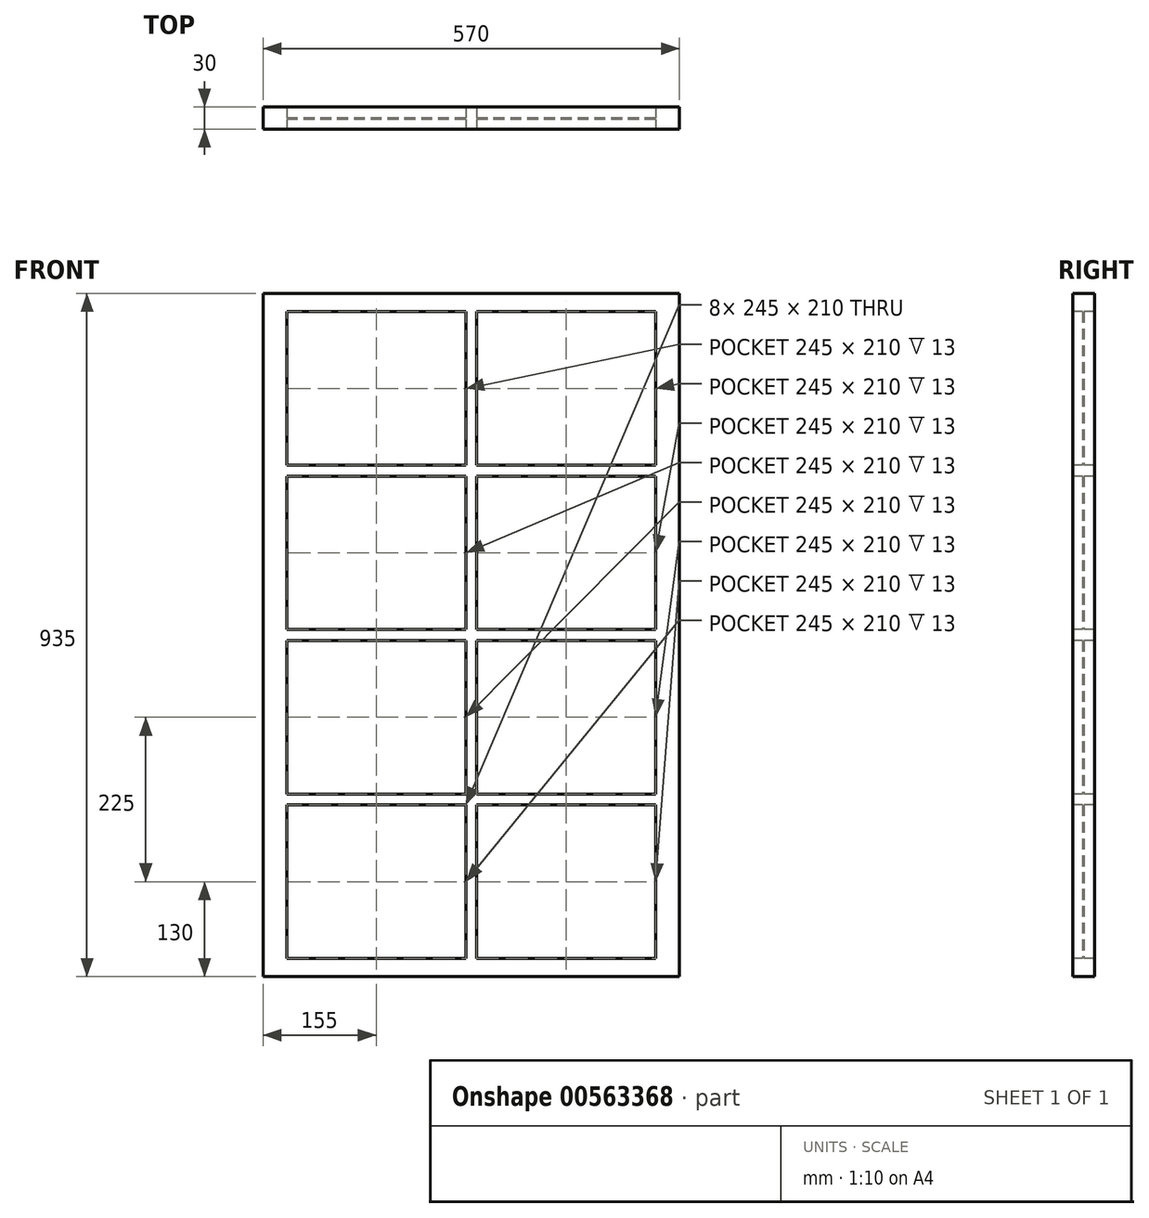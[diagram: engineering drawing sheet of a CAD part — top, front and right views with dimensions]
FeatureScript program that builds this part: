
annotation { "Feature Type Name" : "Feature", "Feature Type Description" : "" }
export const myFeature = defineFeature(function(context is Context, id is Id, definition is map)
    precondition{}
    {
        {
            var Q0;
            Q0=qCreatedBy(makeId("Front.planeOp"),FACE);
            var sketch = newSketch(context, id + "F0", { "sketchPlane" : qUnion([Q0])});
            skLineSegment(sketch, "E0.bottom", {"start": v(-285, 467.5) * mm, "end": v(285, 467.5) * mm});
            skLineSegment(sketch, "E0.top", {"start": v(-285, -467.5) * mm, "end": v(285, -467.5) * mm});
            skLineSegment(sketch, "E0.left", {"start": v(-285, 467.5) * mm, "end": v(-285, -467.5) * mm});
            skLineSegment(sketch, "E0.right", {"start": v(285, 467.5) * mm, "end": v(285, -467.5) * mm});
            skPoint(sketch, "E0.middle", {"position": v(0, 0) * mm});
            skLineSegment(sketch, "E1.bottom", {"start": v(-7.5, 442.5) * mm, "end": v(-252.5, 442.5) * mm});
            skLineSegment(sketch, "E1.top", {"start": v(-7.5, 232.5) * mm, "end": v(-252.5, 232.5) * mm});
            skLineSegment(sketch, "E1.left", {"start": v(-7.5, 442.5) * mm, "end": v(-7.5, 232.5) * mm});
            skLineSegment(sketch, "E1.right", {"start": v(-252.5, 442.5) * mm, "end": v(-252.5, 232.5) * mm});
            skPoint(sketch, "E1.middle", {"position": v(-130, 337.5) * mm});
            skLineSegment(sketch, "E2.0.1.0", {"start": v(-7.5, 217.5) * mm, "end": v(-252.5, 217.5) * mm});
            skLineSegment(sketch, "E2.0.1.1", {"start": v(-252.5, 217.5) * mm, "end": v(-252.5, 7.5) * mm});
            skLineSegment(sketch, "E2.0.1.2", {"start": v(-7.5, 217.5) * mm, "end": v(-7.5, 7.5) * mm});
            skLineSegment(sketch, "E2.0.1.3", {"start": v(-7.5, 7.5) * mm, "end": v(-252.5, 7.5) * mm});
            skLineSegment(sketch, "E2.0.2.0", {"start": v(-7.5, -7.5) * mm, "end": v(-252.5, -7.5) * mm});
            skLineSegment(sketch, "E2.0.2.1", {"start": v(-252.5, -7.5) * mm, "end": v(-252.5, -217.5) * mm});
            skLineSegment(sketch, "E2.0.2.2", {"start": v(-7.5, -7.5) * mm, "end": v(-7.5, -217.5) * mm});
            skLineSegment(sketch, "E2.0.2.3", {"start": v(-7.5, -217.5) * mm, "end": v(-252.5, -217.5) * mm});
            skLineSegment(sketch, "E2.0.3.0", {"start": v(-7.5, -232.5) * mm, "end": v(-252.5, -232.5) * mm});
            skLineSegment(sketch, "E2.0.3.1", {"start": v(-252.5, -232.5) * mm, "end": v(-252.5, -442.5) * mm});
            skLineSegment(sketch, "E2.0.3.2", {"start": v(-7.5, -232.5) * mm, "end": v(-7.5, -442.5) * mm});
            skLineSegment(sketch, "E2.0.3.3", {"start": v(-7.5, -442.5) * mm, "end": v(-252.5, -442.5) * mm});
            skLineSegment(sketch, "E2.1.0.0", {"start": v(252.5, 442.5) * mm, "end": v(7.5, 442.5) * mm});
            skLineSegment(sketch, "E2.1.0.1", {"start": v(7.5, 442.5) * mm, "end": v(7.5, 232.5) * mm});
            skLineSegment(sketch, "E2.1.0.2", {"start": v(252.5, 442.5) * mm, "end": v(252.5, 232.5) * mm});
            skLineSegment(sketch, "E2.1.0.3", {"start": v(252.5, 232.5) * mm, "end": v(7.5, 232.5) * mm});
            skLineSegment(sketch, "E2.1.1.0", {"start": v(252.5, 217.5) * mm, "end": v(7.5, 217.5) * mm});
            skLineSegment(sketch, "E2.1.1.1", {"start": v(7.5, 217.5) * mm, "end": v(7.5, 7.5) * mm});
            skLineSegment(sketch, "E2.1.1.2", {"start": v(252.5, 217.5) * mm, "end": v(252.5, 7.5) * mm});
            skLineSegment(sketch, "E2.1.1.3", {"start": v(252.5, 7.5) * mm, "end": v(7.5, 7.5) * mm});
            skLineSegment(sketch, "E2.1.2.0", {"start": v(252.5, -7.5) * mm, "end": v(7.5, -7.5) * mm});
            skLineSegment(sketch, "E2.1.2.1", {"start": v(7.5, -7.5) * mm, "end": v(7.5, -217.5) * mm});
            skLineSegment(sketch, "E2.1.2.2", {"start": v(252.5, -7.5) * mm, "end": v(252.5, -217.5) * mm});
            skLineSegment(sketch, "E2.1.2.3", {"start": v(252.5, -217.5) * mm, "end": v(7.5, -217.5) * mm});
            skLineSegment(sketch, "E2.1.3.0", {"start": v(252.5, -232.5) * mm, "end": v(7.5, -232.5) * mm});
            skLineSegment(sketch, "E2.1.3.1", {"start": v(7.5, -232.5) * mm, "end": v(7.5, -442.5) * mm});
            skLineSegment(sketch, "E2.1.3.2", {"start": v(252.5, -232.5) * mm, "end": v(252.5, -442.5) * mm});
            skLineSegment(sketch, "E2.1.3.3", {"start": v(252.5, -442.5) * mm, "end": v(7.5, -442.5) * mm});
            skLineSegment(sketch, "E2.direction1", {"start": v(-252.5, 232.5) * mm, "end": v(7.5, 232.5) * mm, "construction": true});
            skLineSegment(sketch, "E2.direction2", {"start": v(-252.5, 232.5) * mm, "end": v(-252.5, 7.5) * mm, "construction": true});
            skSolve(sketch);
        }
        {
            var Q0;
            Q0=makeQuery(id+"F0.imprint","IMPRINT",FACE,{"disambiguationData":[TD([[makeQuery(id+"F0.imprint","IMPRINT",EDGE,{"derivedFrom":sQuery(id+"F0.wireOp",EDGE,"E0.bottom")}),-1.0]])]});
            extrude(context, id + "F1", {"entities" : qUnion([Q0]), "oppositeDirection" : true, "depth" : 30 * mm, "offsetDistance" : 25 * mm});
        }
        {
            var Q0;
            Q0=makeQuery(id+"F1.opExtrude","CAP_FACE",FACE,{"disambiguationData":[OSD([sQuery(id+"F0.wireOp",EDGE,"E0.bottom"),sQuery(id+"F0.wireOp",EDGE,"E0.top"),sQuery(id+"F0.wireOp",EDGE,"E0.left"),sQuery(id+"F0.wireOp",EDGE,"E0.right"),sQuery(id+"F0.wireOp",EDGE,"E1.bottom"),sQuery(id+"F0.wireOp",EDGE,"E1.top"),sQuery(id+"F0.wireOp",EDGE,"E1.left"),sQuery(id+"F0.wireOp",EDGE,"E1.right"),sQuery(id+"F0.wireOp",EDGE,"E2.0.1.0"),sQuery(id+"F0.wireOp",EDGE,"E2.0.1.1"),sQuery(id+"F0.wireOp",EDGE,"E2.0.1.2"),sQuery(id+"F0.wireOp",EDGE,"E2.0.1.3"),sQuery(id+"F0.wireOp",EDGE,"E2.0.2.0"),sQuery(id+"F0.wireOp",EDGE,"E2.0.2.1"),sQuery(id+"F0.wireOp",EDGE,"E2.0.2.2"),sQuery(id+"F0.wireOp",EDGE,"E2.0.2.3"),sQuery(id+"F0.wireOp",EDGE,"E2.0.3.0"),sQuery(id+"F0.wireOp",EDGE,"E2.0.3.1"),sQuery(id+"F0.wireOp",EDGE,"E2.0.3.2"),sQuery(id+"F0.wireOp",EDGE,"E2.0.3.3"),sQuery(id+"F0.wireOp",EDGE,"E2.1.0.0"),sQuery(id+"F0.wireOp",EDGE,"E2.1.0.1"),sQuery(id+"F0.wireOp",EDGE,"E2.1.0.2"),sQuery(id+"F0.wireOp",EDGE,"E2.1.0.3"),sQuery(id+"F0.wireOp",EDGE,"E2.1.1.0"),sQuery(id+"F0.wireOp",EDGE,"E2.1.1.1"),sQuery(id+"F0.wireOp",EDGE,"E2.1.1.2"),sQuery(id+"F0.wireOp",EDGE,"E2.1.1.3"),sQuery(id+"F0.wireOp",EDGE,"E2.1.2.0"),sQuery(id+"F0.wireOp",EDGE,"E2.1.2.1"),sQuery(id+"F0.wireOp",EDGE,"E2.1.2.2"),sQuery(id+"F0.wireOp",EDGE,"E2.1.2.3"),sQuery(id+"F0.wireOp",EDGE,"E2.1.3.0"),sQuery(id+"F0.wireOp",EDGE,"E2.1.3.1"),sQuery(id+"F0.wireOp",EDGE,"E2.1.3.2"),sQuery(id+"F0.wireOp",EDGE,"E2.1.3.3")])],"isStart":true});
            cPlane(context, id + "F2", {"entities" : qUnion([Q0]), "cplaneType" : CPlaneType.OFFSET, "offset" : 15 * mm, "oppositeDirection" : true, "width" : 150 * mm, "height" : 150 * mm});
        }
        {
            var Q0;
            Q0=qCreatedBy(id+"F2.planeOp",FACE);
            var sketch = newSketch(context, id + "F3", { "sketchPlane" : qUnion([Q0])});
            skLineSegment(sketch, "E3.0", {"start": v(-252.5, 442.5) * mm, "end": v(-252.5, 232.5) * mm});
            skLineSegment(sketch, "E4.0", {"start": v(-7.5, 442.5) * mm, "end": v(-252.5, 442.5) * mm});
            skLineSegment(sketch, "E5.0", {"start": v(-7.5, 442.5) * mm, "end": v(-7.5, 232.5) * mm});
            skLineSegment(sketch, "E6.0", {"start": v(-7.5, 232.5) * mm, "end": v(-252.5, 232.5) * mm});
            skLineSegment(sketch, "E7.0", {"start": v(252.5, 232.5) * mm, "end": v(7.5, 232.5) * mm});
            skLineSegment(sketch, "E8.0", {"start": v(7.5, 442.5) * mm, "end": v(7.5, 232.5) * mm});
            skLineSegment(sketch, "E9.0", {"start": v(252.5, 442.5) * mm, "end": v(7.5, 442.5) * mm});
            skLineSegment(sketch, "E10.0", {"start": v(252.5, 442.5) * mm, "end": v(252.5, 232.5) * mm});
            skLineSegment(sketch, "E11.0", {"start": v(252.5, 7.5) * mm, "end": v(7.5, 7.5) * mm});
            skLineSegment(sketch, "E12.0", {"start": v(7.5, 217.5) * mm, "end": v(7.5, 7.5) * mm});
            skLineSegment(sketch, "E13.0", {"start": v(252.5, 217.5) * mm, "end": v(7.5, 217.5) * mm});
            skLineSegment(sketch, "E14.0", {"start": v(252.5, 217.5) * mm, "end": v(252.5, 7.5) * mm});
            skLineSegment(sketch, "E15.0", {"start": v(-7.5, 7.5) * mm, "end": v(-252.5, 7.5) * mm});
            skLineSegment(sketch, "E16.0", {"start": v(-252.5, 217.5) * mm, "end": v(-252.5, 7.5) * mm});
            skLineSegment(sketch, "E17.0", {"start": v(-7.5, 217.5) * mm, "end": v(-252.5, 217.5) * mm});
            skLineSegment(sketch, "E18.0", {"start": v(-7.5, 217.5) * mm, "end": v(-7.5, 7.5) * mm});
            skLineSegment(sketch, "E19.0", {"start": v(-7.5, -7.5) * mm, "end": v(-252.5, -7.5) * mm});
            skLineSegment(sketch, "E20.0", {"start": v(-252.5, -7.5) * mm, "end": v(-252.5, -217.5) * mm});
            skLineSegment(sketch, "E21.0", {"start": v(-7.5, -217.5) * mm, "end": v(-252.5, -217.5) * mm});
            skLineSegment(sketch, "E22.0", {"start": v(-7.5, -7.5) * mm, "end": v(-7.5, -217.5) * mm});
            skLineSegment(sketch, "E23.0", {"start": v(252.5, -217.5) * mm, "end": v(7.5, -217.5) * mm});
            skLineSegment(sketch, "E24.0", {"start": v(7.5, -7.5) * mm, "end": v(7.5, -217.5) * mm});
            skLineSegment(sketch, "E25.0", {"start": v(252.5, -7.5) * mm, "end": v(7.5, -7.5) * mm});
            skLineSegment(sketch, "E26.0", {"start": v(252.5, -7.5) * mm, "end": v(252.5, -217.5) * mm});
            skLineSegment(sketch, "E27.0", {"start": v(252.5, -232.5) * mm, "end": v(252.5, -442.5) * mm});
            skLineSegment(sketch, "E28.0", {"start": v(252.5, -442.5) * mm, "end": v(7.5, -442.5) * mm});
            skLineSegment(sketch, "E29.0", {"start": v(7.5, -232.5) * mm, "end": v(7.5, -442.5) * mm});
            skLineSegment(sketch, "E30.0", {"start": v(252.5, -232.5) * mm, "end": v(7.5, -232.5) * mm});
            skLineSegment(sketch, "E31.0", {"start": v(-7.5, -232.5) * mm, "end": v(-252.5, -232.5) * mm});
            skLineSegment(sketch, "E32.0", {"start": v(-7.5, -232.5) * mm, "end": v(-7.5, -442.5) * mm});
            skLineSegment(sketch, "E33.0", {"start": v(-7.5, -442.5) * mm, "end": v(-252.5, -442.5) * mm});
            skLineSegment(sketch, "E34.0", {"start": v(-252.5, -232.5) * mm, "end": v(-252.5, -442.5) * mm});
            skSolve(sketch);
        }
        {
            var Q0;
            Q0=makeQuery(id+"F3.imprint","IMPRINT",FACE,{"disambiguationData":[TD([[makeQuery(id+"F3.imprint","IMPRINT",EDGE,{"derivedFrom":sQuery(id+"F3.wireOp",EDGE,"E3.0")}),1.0]])]});
            var Q1;
            Q1=makeQuery(id+"F3.imprint","IMPRINT",FACE,{"disambiguationData":[TD([[makeQuery(id+"F3.imprint","IMPRINT",EDGE,{"derivedFrom":sQuery(id+"F3.wireOp",EDGE,"E7.0")}),-1.0]])]});
            var Q2;
            Q2=makeQuery(id+"F3.imprint","IMPRINT",FACE,{"disambiguationData":[TD([[makeQuery(id+"F3.imprint","IMPRINT",EDGE,{"derivedFrom":sQuery(id+"F3.wireOp",EDGE,"E11.0")}),-1.0]])]});
            var Q3;
            Q3=makeQuery(id+"F3.imprint","IMPRINT",FACE,{"disambiguationData":[TD([[makeQuery(id+"F3.imprint","IMPRINT",EDGE,{"derivedFrom":sQuery(id+"F3.wireOp",EDGE,"E15.0")}),-1.0]])]});
            var Q4;
            Q4=makeQuery(id+"F3.imprint","IMPRINT",FACE,{"disambiguationData":[TD([[makeQuery(id+"F3.imprint","IMPRINT",EDGE,{"derivedFrom":sQuery(id+"F3.wireOp",EDGE,"E19.0")}),1.0]])]});
            var Q5;
            Q5=makeQuery(id+"F3.imprint","IMPRINT",FACE,{"disambiguationData":[TD([[makeQuery(id+"F3.imprint","IMPRINT",EDGE,{"derivedFrom":sQuery(id+"F3.wireOp",EDGE,"E23.0")}),-1.0]])]});
            var Q6;
            Q6=makeQuery(id+"F3.imprint","IMPRINT",FACE,{"disambiguationData":[TD([[makeQuery(id+"F3.imprint","IMPRINT",EDGE,{"derivedFrom":sQuery(id+"F3.wireOp",EDGE,"E27.0")}),-1.0]])]});
            var Q7;
            Q7=makeQuery(id+"F3.imprint","IMPRINT",FACE,{"disambiguationData":[TD([[makeQuery(id+"F3.imprint","IMPRINT",EDGE,{"derivedFrom":sQuery(id+"F3.wireOp",EDGE,"E32.0")}),-1.0]])]});
            extrude(context, id + "F4", {"entities" : qUnion([Q0, Q1, Q2, Q3, Q4, Q5, Q6, Q7]), "operationType" : NewBodyOperationType.ADD, "depth" : 2 * mm, "offsetDistance" : 25 * mm});
        }
    });
